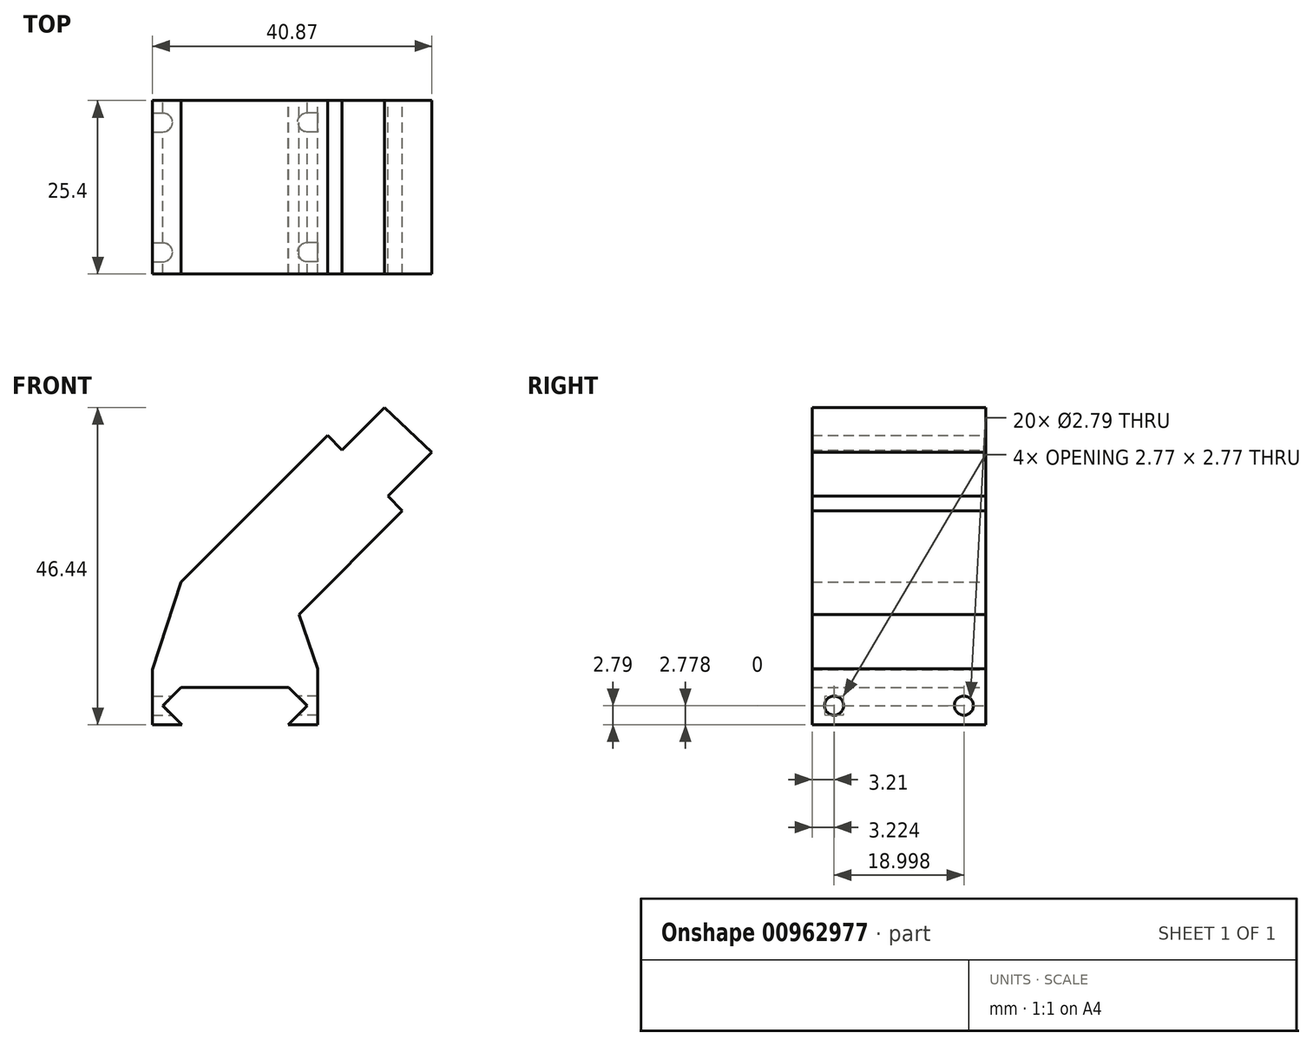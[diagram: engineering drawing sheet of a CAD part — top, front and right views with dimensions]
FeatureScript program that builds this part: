
annotation { "Feature Type Name" : "Feature", "Feature Type Description" : "" }
export const myFeature = defineFeature(function(context is Context, id is Id, definition is map)
    precondition{}
    {
        {
            var Q0;
            Q0=qCreatedBy(makeId("Front.planeOp"),FACE);
            var sketch = newSketch(context, id + "F0", { "sketchPlane" : qUnion([Q0])});
            skLineSegment(sketch, "E0", {"start": v(8.24, -9.31) * mm, "end": v(11, -6.54) * mm});
            skLineSegment(sketch, "E1", {"start": v(11, -6.54) * mm, "end": v(8.23, -3.78) * mm});
            skLineSegment(sketch, "E2.MirrorCS", {"start": v(-10.13, -6.54) * mm, "end": v(-7.35, -3.78) * mm});
            skLineSegment(sketch, "E3.MirrorCS", {"start": v(-7.36, -9.3) * mm, "end": v(-10.13, -6.54) * mm});
            skLineSegment(sketch, "E4.bottom", {"start": v(-7.36, -9.3) * mm, "end": v(-11.63, -9.3) * mm});
            skLineSegment(sketch, "E5.top", {"start": v(8.32, -3.86) * mm, "end": v(-7.44, -3.86) * mm});
            skLineSegment(sketch, "E6.right", {"start": v(-11.63, -1.23) * mm, "end": v(-11.63, -9.3) * mm});
            skLineSegment(sketch, "E7.top", {"start": v(12.55, -9.31) * mm, "end": v(8.24, -9.31) * mm});
            skLineSegment(sketch, "E7.left", {"start": v(12.55, -1.1) * mm, "end": v(12.55, -9.31) * mm});
            skLineSegment(sketch, "E8.right", {"start": v(-7.44, 11.55) * mm, "end": v(-7.44, 11.55) * mm});
            skLineSegment(sketch, "E9", {"start": v(9.8, 6.84) * mm, "end": v(12.55, -1.1) * mm});
            skLineSegment(sketch, "E10", {"start": v(-7.44, 11.55) * mm, "end": v(-11.63, -1.23) * mm});
            skLineSegment(sketch, "E11.left", {"start": v(-7.44, 11.55) * mm, "end": v(14.03, 33.02) * mm});
            skLineSegment(sketch, "E11.right", {"start": v(9.8, 6.84) * mm, "end": v(24.95, 22) * mm});
            skLineSegment(sketch, "E12.left", {"start": v(14.03, 33.02) * mm, "end": v(13.98, 32.97) * mm});
            skLineSegment(sketch, "E12.right", {"start": v(22.32, 37.13) * mm, "end": v(16.07, 30.88) * mm});
            skLineSegment(sketch, "E13.left", {"start": v(29.24, 30.58) * mm, "end": v(22.8, 24.14) * mm});
            skLineSegment(sketch, "E14.trimOffspring", {"start": v(-7.44, -1.2) * mm, "end": v(-7.44, -1.21) * mm});
            skPoint(sketch, "E15.top.end.orphan", {"position": v(-7.44, 8.88) * mm});
            skLineSegment(sketch, "E16", {"start": v(22.32, 37.13) * mm, "end": v(29.24, 30.58) * mm});
            skLineSegment(sketch, "E17", {"start": v(16.07, 30.88) * mm, "end": v(14.03, 33.02) * mm});
            skLineSegment(sketch, "E18", {"start": v(22.8, 24.14) * mm, "end": v(24.95, 22) * mm});
            skSolve(sketch);
        }
        {
            var Q0;
            {var subQ8=sQuery(id+"F0.wireOp",EDGE,"E8.right");Q0=makeQuery(id+"F0.imprint","IMPRINT",FACE,{"disambiguationData":[TD([[makeQuery(id+"F0.imprint","IMPRINT",EDGE,{"derivedFrom":subQ8}),1.0]])]});}
            var Q1;
            {var subQ6=sQuery(id+"F0.wireOp",EDGE,"E0");Q1=makeQuery(id+"F0.imprint","IMPRINT",FACE,{"disambiguationData":[TD([[makeQuery(id+"F0.imprint","IMPRINT",EDGE,{"derivedFrom":subQ6}),-1.0]])]});}
            var Q2;
            Q2=makeQuery(id+"F0.imprint","IMPRINT",FACE,{"disambiguationData":[TD([[makeQuery(id+"F0.imprint","IMPRINT",EDGE,{"derivedFrom":sQuery(id+"F0.wireOp",EDGE,"E12.bottom")}),-1.0]])]});
            var Q3;
            Q3=makeQuery(id+"F0.imprint","IMPRINT",FACE,{"disambiguationData":[TD([[makeQuery(id+"F0.imprint","IMPRINT",EDGE,{"derivedFrom":sQuery(id+"F0.wireOp",EDGE,"E13.bottom")}),-1.0]])]});
            extrude(context, id + "F1", {"entities" : qUnion([Q0, Q1, Q2, Q3]), "depth" : 25.4 * mm, "offsetDistance" : 25.4 * mm});
        }
        {
            var Q0;
            Q0=qCreatedBy(makeId("Right.planeOp"),FACE);
            var sketch = newSketch(context, id + "F2", { "sketchPlane" : qUnion([Q0])});
            skPoint(sketch, "E19", {"position": v(-22.19, -6.52) * mm});
            skPoint(sketch, "E20", {"position": v(-3.2, -6.52) * mm});
            skSolve(sketch);
        }
        {
            var Q0;
            Q0=sQuery(id+"F2.wireOp",VERTEX,"E19");
            var Q1;
            Q1=sQuery(id+"F2.wireOp",VERTEX,"E20");
            var Q2;
            Q2=makeQuery(id+"F1.opExtrude","SWEPT_BODY",BODY,{"disambiguationData":[OSD([sQuery(id+"F0.wireOp",EDGE,"E0"),sQuery(id+"F0.wireOp",EDGE,"E1"),sQuery(id+"F0.wireOp",EDGE,"E2.MirrorCS"),sQuery(id+"F0.wireOp",EDGE,"E3.MirrorCS"),sQuery(id+"F0.wireOp",EDGE,"E4.bottom"),sQuery(id+"F0.wireOp",EDGE,"E5.top"),sQuery(id+"F0.wireOp",EDGE,"E6.right"),sQuery(id+"F0.wireOp",EDGE,"E7.top"),sQuery(id+"F0.wireOp",EDGE,"E7.left"),sQuery(id+"F0.wireOp",EDGE,"E8.right"),sQuery(id+"F0.wireOp",EDGE,"E9"),sQuery(id+"F0.wireOp",EDGE,"E10"),sQuery(id+"F0.wireOp",EDGE,"E11.top"),sQuery(id+"F0.wireOp",EDGE,"E11.left"),sQuery(id+"F0.wireOp",EDGE,"E11.right"),sQuery(id+"F0.wireOp",EDGE,"E12.bottom"),sQuery(id+"F0.wireOp",EDGE,"E12.left"),sQuery(id+"F0.wireOp",EDGE,"E12.right"),sQuery(id+"F0.wireOp",EDGE,"E13.bottom"),sQuery(id+"F0.wireOp",EDGE,"E13.left"),sQuery(id+"F0.wireOp",EDGE,"E13.right"),sQuery(id+"F0.wireOp",EDGE,"E8.right")])]});
            hole(context, id + "F3", {"style" : HoleStyle.SIMPLE, "endStyle" : HoleEndStyle.BLIND, "oppositeDirection" : true, "holeDiameter" : 2.8 * mm, "majorDiameter" : 6.35 * mm, "holeDepth" : 25.4 * mm, "isTappedThrough" : true, "tappedDepth" : 12.7 * mm, "tapClearance" : 3, "locations" : qUnion([Q0, Q1]), "scope" : qUnion([Q2])});
        }
        {
            var Q0;
            Q0=sQuery(id+"F2.wireOp",VERTEX,"E20");
            var Q1;
            Q1=sQuery(id+"F2.wireOp",VERTEX,"E19");
            var Q2;
            Q2=makeQuery(id+"F1.opExtrude","SWEPT_BODY",BODY,{"disambiguationData":[OSD([sQuery(id+"F0.wireOp",EDGE,"E0"),sQuery(id+"F0.wireOp",EDGE,"E1"),sQuery(id+"F0.wireOp",EDGE,"E2.MirrorCS"),sQuery(id+"F0.wireOp",EDGE,"E3.MirrorCS"),sQuery(id+"F0.wireOp",EDGE,"E4.bottom"),sQuery(id+"F0.wireOp",EDGE,"E5.top"),sQuery(id+"F0.wireOp",EDGE,"E6.right"),sQuery(id+"F0.wireOp",EDGE,"E7.top"),sQuery(id+"F0.wireOp",EDGE,"E7.left"),sQuery(id+"F0.wireOp",EDGE,"E8.right"),sQuery(id+"F0.wireOp",EDGE,"E9"),sQuery(id+"F0.wireOp",EDGE,"E10"),sQuery(id+"F0.wireOp",EDGE,"E11.top"),sQuery(id+"F0.wireOp",EDGE,"E11.left"),sQuery(id+"F0.wireOp",EDGE,"E11.right"),sQuery(id+"F0.wireOp",EDGE,"E12.bottom"),sQuery(id+"F0.wireOp",EDGE,"E12.left"),sQuery(id+"F0.wireOp",EDGE,"E12.right"),sQuery(id+"F0.wireOp",EDGE,"E13.bottom"),sQuery(id+"F0.wireOp",EDGE,"E13.left"),sQuery(id+"F0.wireOp",EDGE,"E13.right"),sQuery(id+"F0.wireOp",EDGE,"E8.right")])]});
            hole(context, id + "F4", {"style" : HoleStyle.SIMPLE, "endStyle" : HoleEndStyle.BLIND, "holeDiameter" : 2.8 * mm, "majorDiameter" : 6.35 * mm, "holeDepth" : 25.4 * mm, "isTappedThrough" : true, "tappedDepth" : 12.7 * mm, "tapClearance" : 3, "locations" : qUnion([Q0, Q1]), "scope" : qUnion([Q2])});
        }
    });
